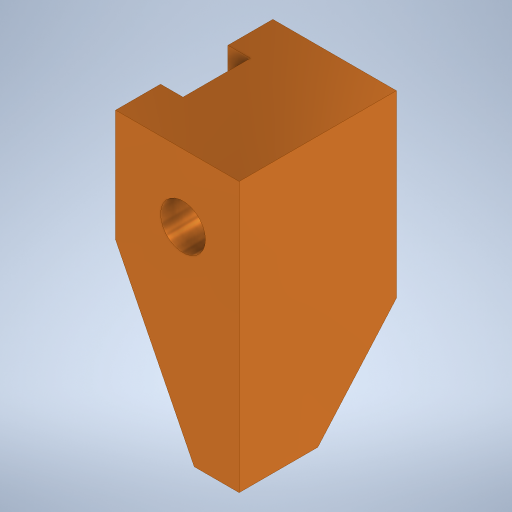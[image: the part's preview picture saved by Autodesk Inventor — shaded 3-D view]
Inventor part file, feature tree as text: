
AUTODESK INVENTOR PART (.ipt)
format: ipt  version: 2024 (Build 280153000, 153)  size: 235,520 bytes
history: native  units: in
note: dims shown in document units (in); Inventor stores cm internally (conversion verified against a paired STEP export)
features: chamfer x2, sketch x2, extrude x1, hole x1
ambient origin geometry x8: Origin, YZ Plane, XZ Plane, XY Plane, X Axis, Y Axis, Z Axis, Center Point
bodies: Solid1 (feature_tree)
feature tree (6):
  extrude  "NOTCHED SHAPE"  Depth=2.75in
  chamfer  "TOP SURF"  Distance=1.5in
  chamfer  "EDGE SURF"  Distance=0.75in
  hole  "Hole1"  [1 undecoded]
  sketch  "Sketch1"  dims[d0=3.5in d1=2.75in]
  sketch  "Sketch2"  dims[d3=0.5in d4=1.5in d5=0.75in d6=0.0in d7=1.75in d8=6.0in d9=0.0in d10=3.5in d11=1.75in d12=45.0deg d13=1.75in d14=2.0in d15=45.0deg d16=1.5in d17=1.25in d18=1.0in d19=0.75in d20=0.375in d21=0.25in d22=0.5635in d23=1.0in d24=0.8108in]
note: 1 required parameter value undecoded (feature->parameter linkage not recoverable at this tier; creation-order binding heuristic only, values carry confidence <= 0.55)
